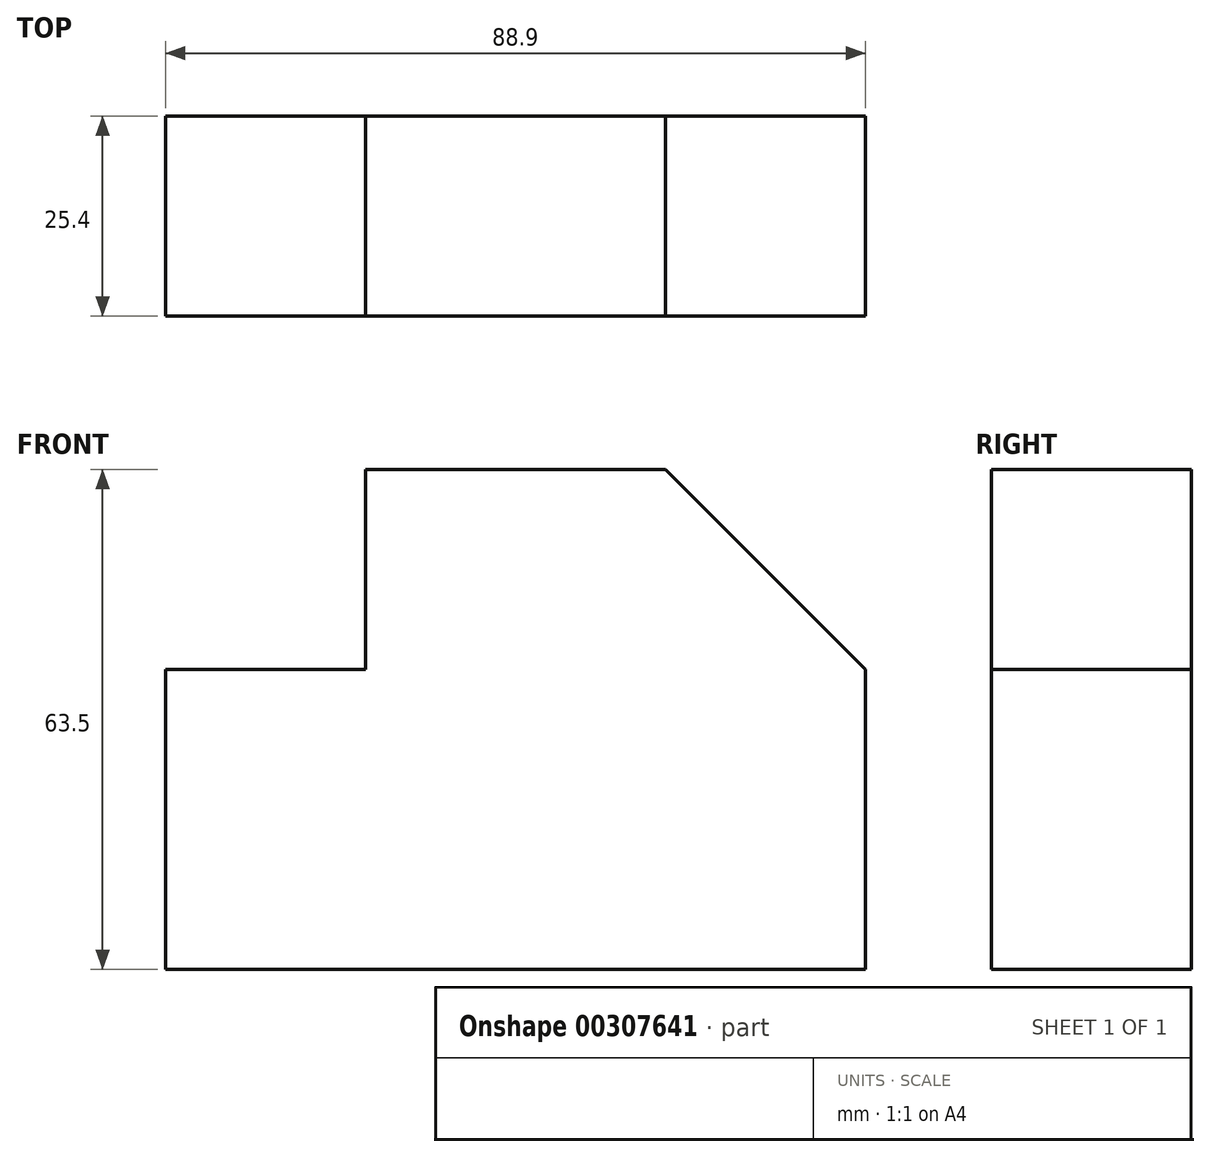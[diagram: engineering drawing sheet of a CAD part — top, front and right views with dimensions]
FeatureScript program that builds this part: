
annotation { "Feature Type Name" : "Feature", "Feature Type Description" : "" }
export const myFeature = defineFeature(function(context is Context, id is Id, definition is map)
    precondition{}
    {
        {
            var Q0;
            Q0=qCreatedBy(makeId("Front.planeOp"),FACE);
            var sketch = newSketch(context, id + "F0", { "sketchPlane" : qUnion([Q0])});
            skLineSegment(sketch, "E0", {"start": v(-51.57, -60.53) * mm, "end": v(37.33, -60.53) * mm});
            skLineSegment(sketch, "E1", {"start": v(37.33, -60.53) * mm, "end": v(37.33, -22.43) * mm});
            skLineSegment(sketch, "E2", {"start": v(-51.57, -60.53) * mm, "end": v(-51.57, -22.43) * mm});
            skLineSegment(sketch, "E3", {"start": v(-51.57, -22.43) * mm, "end": v(-26.17, -22.43) * mm});
            skLineSegment(sketch, "E4", {"start": v(-26.17, -22.43) * mm, "end": v(-26.17, 2.97) * mm});
            skLineSegment(sketch, "E5", {"start": v(-26.17, 2.97) * mm, "end": v(11.93, 2.97) * mm});
            skLineSegment(sketch, "E6", {"start": v(11.93, 2.97) * mm, "end": v(37.33, -22.43) * mm});
            skSolve(sketch);
        }
        {
            var Q0;
            Q0=makeQuery(id+"F0.imprint","IMPRINT",FACE,{"disambiguationData":[TD([[makeQuery(id+"F0.imprint","IMPRINT",EDGE,{"derivedFrom":sQuery(id+"F0.wireOp",EDGE,"E0")}),1.0]])]});
            extrude(context, id + "F1", {"entities" : qUnion([Q0]), "depth" : 25.4 * mm});
        }
    });
